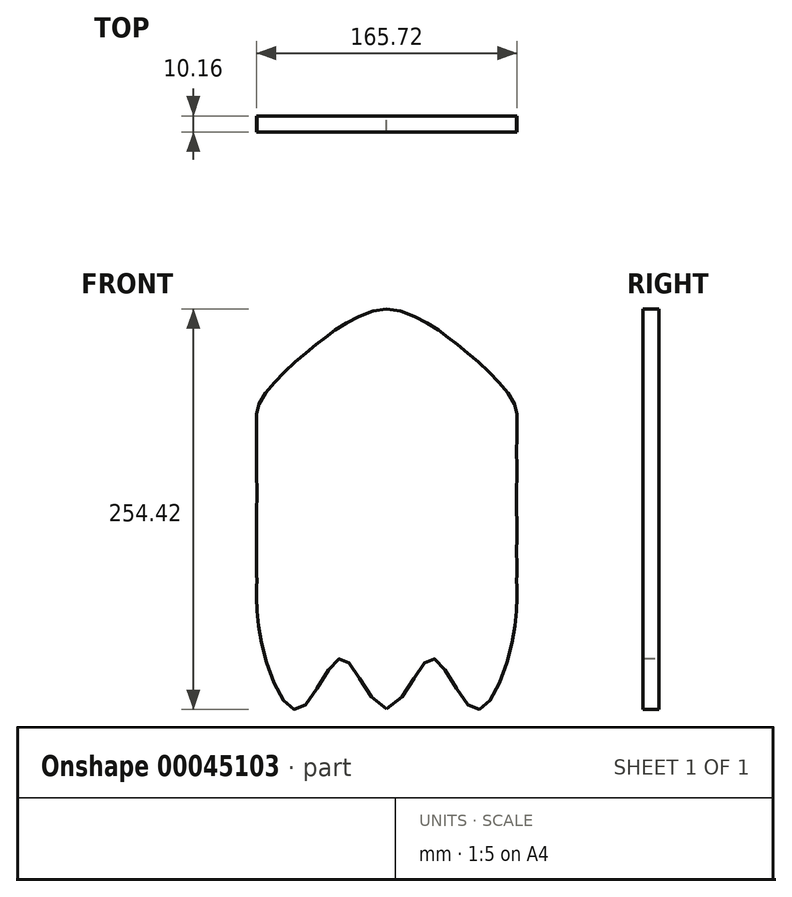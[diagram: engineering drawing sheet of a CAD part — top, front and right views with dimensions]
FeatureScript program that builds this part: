
annotation { "Feature Type Name" : "Feature", "Feature Type Description" : "" }
export const myFeature = defineFeature(function(context is Context, id is Id, definition is map)
    precondition{}
    {
        {
            var Q0;
            Q0=qCreatedBy(makeId("Front.planeOp"),FACE);
            var sketch = newSketch(context, id + "F0", { "sketchPlane" : qUnion([Q0])});
            skLineSegment(sketch, "E0.rect.bottom", {"start": v(82.55, 127) * mm, "end": v(-82.55, 127) * mm, "construction": true});
            skLineSegment(sketch, "E0.rect.top", {"start": v(82.55, -127) * mm, "end": v(-82.55, -127) * mm, "construction": true});
            skLineSegment(sketch, "E0.rect.left", {"start": v(82.55, 127) * mm, "end": v(82.55, -127) * mm, "construction": true});
            skLineSegment(sketch, "E0.rect.right", {"start": v(-82.55, 127) * mm, "end": v(-82.55, -127) * mm, "construction": true});
            skPoint(sketch, "E0.rect.middle", {"position": v(0, 0) * mm});
            skLineSegment(sketch, "E1", {"start": v(-82.55, 0) * mm, "end": v(82.55, 0) * mm, "construction": true});
            skLineSegment(sketch, "E2", {"start": v(0, -127) * mm, "end": v(0, 127) * mm, "construction": true});
            skFitSpline(sketch, "E3", {"points": [v(-82.55, 0) * mm, v(-82.55, 15.27) * mm, v(-82.55, 35.23) * mm, v(-82.55, 37.08) * mm, v(-82.55, 55.56) * mm, v(-82.55, 55.66) * mm, v(-82.55, 62.59) * mm, v(-68.8, 83.16) * mm, v(-46.8, 102.92) * mm, v(-28.3, 116.43) * mm, v(0, 127) * mm], "startDerivative": vector(0.49, 242.61) * mm, "endDerivative": vector(201.59, 0) * mm});
            skFitSpline(sketch, "E4.MirrorCS", {"points": [v(82.55, 0) * mm, v(82.55, 15.27) * mm, v(82.55, 35.23) * mm, v(82.55, 37.08) * mm, v(82.55, 55.56) * mm, v(82.55, 55.66) * mm, v(82.55, 62.59) * mm, v(68.8, 83.16) * mm, v(46.8, 102.92) * mm, v(28.3, 116.43) * mm, v(0, 127) * mm], "startDerivative": vector(-0.49, 242.61) * mm, "endDerivative": vector(-201.59, 0) * mm});
            skFitSpline(sketch, "E5", {"points": [v(-82.55, 0) * mm, v(-82.55, -26.94) * mm, v(-82.55, -43.11) * mm, v(-82.55, -46.5) * mm, v(-82.55, -60.33) * mm, v(-76, -98.38) * mm, v(-55.33, -127) * mm, v(-28.82, -94.79) * mm, v(0, -127) * mm], "startDerivative": vector(-1.13, -218.54) * mm, "endDerivative": vector(253.14, -87.17) * mm});
            skFitSpline(sketch, "E6.MirrorCS", {"points": [v(82.55, 0) * mm, v(82.55, -26.94) * mm, v(82.55, -43.11) * mm, v(82.55, -46.5) * mm, v(82.55, -60.33) * mm, v(76, -98.38) * mm, v(55.33, -127) * mm, v(28.82, -94.79) * mm, v(0, -127) * mm], "startDerivative": vector(1.13, -218.54) * mm, "endDerivative": vector(-253.14, -87.17) * mm});
            skFitSpline(sketch, "E7", {"points": [v(-453.45, -35.02) * mm, v(-440.87, -28.28) * mm, v(-445.81, -30.98) * mm], "startDerivative": vector(30.7, 16.49) * mm, "endDerivative": vector(-19.24, -10.45) * mm});
            skSolve(sketch);
        }
        {
            var Q0;
            Q0=makeQuery(id+"F0.imprint","IMPRINT",FACE,{"disambiguationData":[TD([[makeQuery(id+"F0.imprint","IMPRINT",EDGE,{"derivedFrom":sQuery(id+"F0.wireOp",EDGE,"E3")}),-1.0]])]});
            extrude(context, id + "F1", {"entities" : qUnion([Q0]), "depth" : 10.16 * mm});
        }
    });
